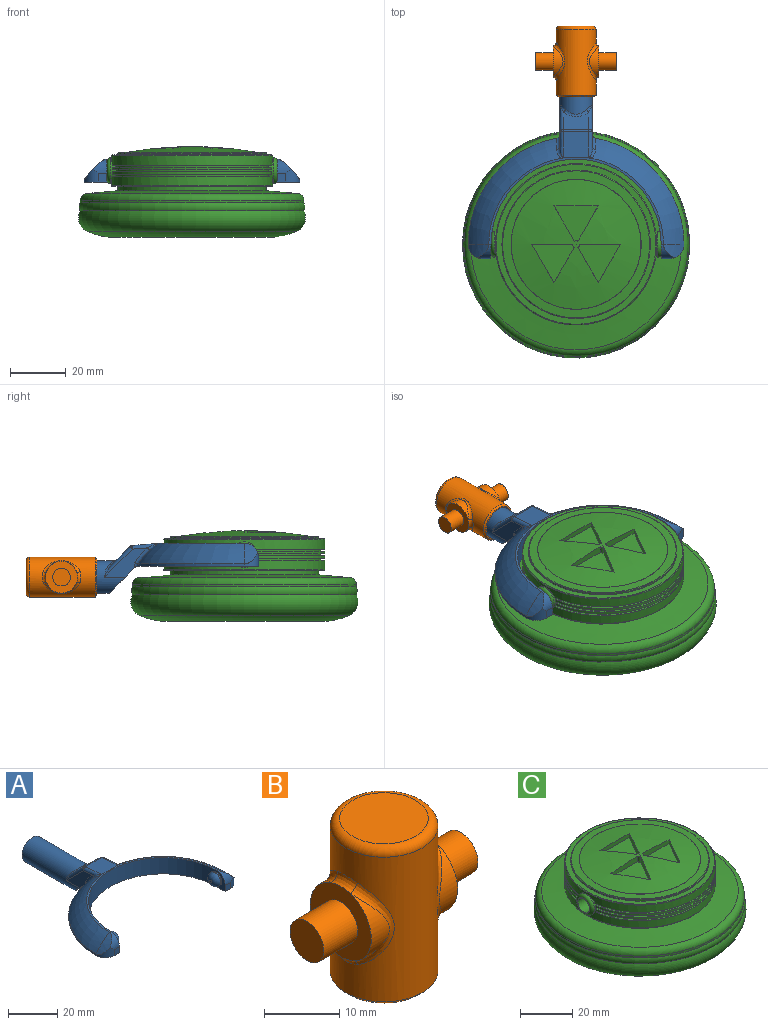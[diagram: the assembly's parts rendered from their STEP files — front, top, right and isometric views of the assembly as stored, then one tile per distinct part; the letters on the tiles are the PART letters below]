
ASSEMBLY  parts=3 mates=2
PART A: 48 faces, bbox 77.3x80.8x18.2 mm
  f0: plane 11.99x9.83mm, normal (0,-0.71,-0.71), area 141.5mm2, adj f1,f2,f9,f30,f43,f46
  f1: plane 15.39x10.49mm, normal (-1,0,0), area 63.5mm2, adj f0,f30,f32,f36,f46,f47
  f2: plane 15.39x10.49mm, normal (1,0,0), area 63.5mm2, adj f0,f30,f34,f39,f43,f44
  f3: plane 9.14x6.37mm, normal (0,0.71,0.71), area 67.6mm2, adj f35,f36,f39,f40
  f4: cylinder r=38.61mm len=37.99mm, axis (0,0,-1), area 42.6mm2, adj f6,f9,f17,f46,f47
  f5: torus R=19.3mm, axis (0,0,-1), area 507.8mm2, adj f10,f11,f12,f29,f42,f44
  f6: torus R=19.3mm, axis (0,0,-1), area 507.8mm2, adj f4,f11,f15,f28,f45,f47
  f7: cylinder r=30.48mm len=60.96mm, axis (0,0,-1), area 746.6mm2, adj f8,f9,f11,f14,f21,f24
  f8: plane 8.13x5.08mm, normal (-1,0,0), area 19.9mm2, adj f7,f9,f13,f19,f24
  f9: plane 77.22x43.73mm, normal (0,0,-1), area 956.2mm2, adj f0,f4,f7,f8,f10,f13,f14,f16
  f10: cylinder r=38.61mm len=37.99mm, axis (0,0,-1), area 42.6mm2, adj f5,f9,f20,f43,f44
  f11: plane 62.55x30.95mm, normal (0,0,1), area 75mm2, adj f5,f6,f7,f18,f19,f27
  f12: cylinder r=22.71mm len=7.33mm, axis (0,1,0), area 24.8mm2, adj f5,f19,f20
  f13: plane 3.05x3.05mm, normal (0,-1,0), area 9.3mm2, adj f8,f9,f19,f20
  f14: plane 8.13x5.08mm, normal (1,0,0), area 19.9mm2, adj f7,f9,f16,f18,f21
  f15: cylinder r=22.71mm len=7.33mm, axis (0,1,0), area 24.8mm2, adj f6,f17,f18
  f16: plane 3.05x3.05mm, normal (0,-1,0), area 9.3mm2, adj f9,f14,f17,f18
  f17: cylinder r=5.08mm len=5.08mm, axis (0,0,-1), area 21.9mm2, adj f4,f9,f15,f16,f18
  f18: cylinder r=5.08mm len=5.08mm, axis (-1,0,0), area 21.9mm2, adj f11,f14,f15,f16,f17
  f19: cylinder r=5.08mm len=5.08mm, axis (-1,0,0), area 21.9mm2, adj f8,f11,f12,f13,f20
  f20: cylinder r=5.08mm len=5.08mm, axis (0,0,-1), area 21.9mm2, adj f9,f10,f12,f13,f19
  f21: cylinder r=3.17mm len=6.35mm, axis (-1,0,0), area 12.7mm2, adj f7,f14,f23
  f22: plane 1.27x1.27mm, normal (1,0,0), area 1.3mm2, adj f23
  f23: torus R=0.64mm, axis (1,0,0), area 56.5mm2, adj f21,f22
  f24: cylinder r=3.17mm len=6.35mm, axis (1,0,0), area 12.7mm2, adj f7,f8,f26
  f25: plane 1.27x1.27mm, normal (-1,0,0), area 1.3mm2, adj f26
  f26: torus R=0.64mm, axis (-1,0,0), area 56.5mm2, adj f24,f25
  f27: plane 9.86x9.36mm, normal (0,0.09,1), area 85.6mm2, adj f11,f28,f29,f32,f34,f35,f42,f45
  f28: plane 1.04x0.17mm, normal (0,-1,0), area 0mm2, adj f6,f27,f45
  f29: plane 1.04x0.17mm, normal (0,-1,0), area 0mm2, adj f5,f27,f42
  f30: cylinder r=5.84mm len=33.01mm, axis (0,-1,0), area 1029.7mm2, adj f0,f1,f2,f31,f38,f40,f41
  f31: plane 11.68x11.68mm, normal (0,1,0), area 107.2mm2, adj f30
  f32: cylinder r=1.27mm len=9.13mm, axis (0,-1,0.09), area 14.4mm2, adj f1,f27,f33,f45
  f33: sphere r=1.27mm, area 1.5mm2, adj f32,f35,f36
  f34: cylinder r=1.27mm len=9.13mm, axis (0,1,-0.09), area 14.4mm2, adj f2,f27,f37,f42
  f35: cylinder r=1.27mm len=9.14mm, axis (-1,0,0), area 8.1mm2, adj f3,f27,f33,f37
  f36: cylinder r=1.27mm len=10.91mm, axis (0,-0.71,0.71), area 23.1mm2, adj f1,f3,f33,f38
  f37: sphere r=1.27mm, area 1.5mm2, adj f34,f35,f39
  f38: bspline ~4.55x2.75mm, area 2.3mm2, adj f30,f36,f40
  f39: cylinder r=1.27mm len=10.91mm, axis (0,0.71,-0.71), area 23.1mm2, adj f2,f3,f37,f41
  f40: bspline ~9.14x2.56mm, area 10.7mm2, adj f3,f30,f38,f41
  f41: bspline ~5.23x3.53mm, area 2.3mm2, adj f30,f39,f40
  f42: bspline ~4.62x3.14mm, area 5.2mm2, adj f5,f27,f29,f34,f44
  f43: cylinder r=1.27mm len=1.74mm, axis (0,0,-1), area 1.9mm2, adj f0,f2,f9,f10,f44
  f44: bspline ~8.6x7.86mm, area 11.9mm2, adj f2,f5,f10,f42,f43
  f45: bspline ~4.62x3.14mm, area 5.2mm2, adj f6,f27,f28,f32,f47
  f46: cylinder r=1.27mm len=1.74mm, axis (0,0,-1), area 1.9mm2, adj f0,f1,f4,f9,f47
  f47: bspline ~8.6x7.86mm, area 11.9mm2, adj f1,f4,f6,f45,f46
PART B: 25 faces, bbox 28.9x15.5x25.4 mm
  f0: cylinder r=5.71mm len=10.81mm, axis (-1,0,0), area 26.2mm2, adj f5,f15
  f1: cylinder r=5.71mm len=10.81mm, axis (-1,0,0), area 26.2mm2, adj f8,f11
  f2: cylinder r=7.14mm len=23.5mm, axis (0,0,-1), area 763.2mm2, adj f9,f10,f11,f12,f13,f14,f15,f16
  f3: plane 11.75x11.75mm, normal (0,0,1), area 108.4mm2, adj f17
  f4: plane 13.02x13.02mm, normal (0,0,-1), area 16.3mm2, adj f22,f24
  f5: plane 11.46x11.46mm, normal (1,0,0), area 70.9mm2, adj f0,f6,f13,f16,f18
  f6: cylinder r=5.71mm len=10.81mm, axis (-1,0,0), area 26.2mm2, adj f5,f14
  f7: cylinder r=5.71mm len=10.81mm, axis (-1,0,0), area 26.2mm2, adj f8,f10
  f8: plane 11.46x11.46mm, normal (-1,0,0), area 70.9mm2, adj f1,f7,f9,f12,f20
  f9: bspline ~4.64x1.73mm, area 6.5mm2, adj f2,f8,f10,f11
  f10: bspline ~13.62x4.91mm, area 20.7mm2, adj f2,f7,f9,f12
  f11: bspline ~13.6x4.87mm, area 20.7mm2, adj f1,f2,f9,f12
  f12: bspline ~4.64x1.73mm, area 6.5mm2, adj f2,f8,f10,f11
  f13: bspline ~4.64x1.73mm, area 6.5mm2, adj f2,f5,f14,f15
  f14: bspline ~13.62x4.91mm, area 20.7mm2, adj f2,f6,f13,f16
  f15: bspline ~13.6x4.87mm, area 20.7mm2, adj f0,f2,f13,f16
  f16: bspline ~4.64x1.73mm, area 6.5mm2, adj f2,f5,f14,f15
  f17: torus R=5.87mm, axis (0,0,1), area 83.8mm2, adj f2,f3
  f18: cylinder r=3.17mm len=6.35mm, axis (-1,0,0), area 126.7mm2, adj f5,f19
  f19: plane 6.35x6.35mm, normal (1,0,0), area 31.7mm2, adj f18
  f20: cylinder r=3.17mm len=6.35mm, axis (1,0,0), area 126.7mm2, adj f8,f21
  f21: plane 6.35x6.35mm, normal (-1,0,0), area 31.7mm2, adj f20
  f22: cylinder r=6.1mm len=22.86mm, axis (0,0,-1), area 875.6mm2, adj f4,f23
  f23: plane 12.19x12.19mm, normal (0,0,-1), area 116.7mm2, adj f22
  f24: cone r=7.14mm half-angle=45deg, axis (0,0,1), area 38.5mm2, adj f2,f4
PART C: 64 faces, bbox 96.2x96.2x32.5 mm
  f0: cylinder r=28.87mm len=57.73mm, axis (0,0,-1), area 595.7mm2, adj f1,f2,f54,f55,f60
  f1: plane 57.13x24.71mm, normal (0,0,1), area 102mm2, adj f0,f3,f54,f55
  f2: plane 57.13x24.71mm, normal (0,0,1), area 102mm2, adj f0,f4,f54,f55
  f3: cylinder r=27.6mm len=54.56mm, axis (0,0,-1), area 49.6mm2, adj f1,f6,f54,f55
  f4: cylinder r=27.6mm len=54.56mm, axis (0,0,-1), area 49.6mm2, adj f2,f5,f54,f55
  f5: plane 57.06x24.48mm, normal (0,0,-1), area 101.4mm2, adj f4,f8,f54,f55
  f6: plane 57.06x24.48mm, normal (0,0,-1), area 101.4mm2, adj f3,f7,f54,f55
  f7: cylinder r=28.87mm len=57.06mm, axis (0,0,-1), area 77.8mm2, adj f6,f9,f54,f55
  f8: cylinder r=28.87mm len=57.06mm, axis (0,0,-1), area 77.8mm2, adj f5,f10,f54,f55
  f9: plane 57.01x24.31mm, normal (0,0,1), area 101mm2, adj f7,f11,f54,f55
  f10: plane 57.01x24.31mm, normal (0,0,1), area 101mm2, adj f8,f12,f54,f55
  f11: cylinder r=27.6mm len=54.44mm, axis (0,0,-1), area 49.2mm2, adj f9,f13,f54,f55
  f12: cylinder r=27.6mm len=54.44mm, axis (0,0,-1), area 49.2mm2, adj f10,f14,f54,f55
  f13: plane 57.01x24.31mm, normal (0,0,-1), area 101mm2, adj f11,f15,f54,f55
  f14: plane 57.01x24.31mm, normal (0,0,-1), area 101mm2, adj f12,f16,f54,f55
  f15: cylinder r=28.87mm len=57.06mm, axis (0,0,-1), area 77.8mm2, adj f13,f22,f54,f55
  f16: cylinder r=28.87mm len=57.06mm, axis (0,0,-1), area 77.8mm2, adj f14,f21,f54,f55
  f17: cylinder r=27.6mm len=54.56mm, axis (0,0,-1), area 49.6mm2, adj f19,f22,f54,f55
  f18: cylinder r=27.6mm len=54.56mm, axis (0,0,-1), area 49.6mm2, adj f20,f21,f54,f55
  f19: plane 57.13x24.71mm, normal (0,0,-1), area 102mm2, adj f17,f23,f54,f55
  f20: plane 57.13x24.71mm, normal (0,0,-1), area 102mm2, adj f18,f23,f54,f55
  f21: plane 57.06x24.48mm, normal (0,0,1), area 101.4mm2, adj f16,f18,f54,f55
  f22: plane 57.06x24.48mm, normal (0,0,1), area 101.4mm2, adj f15,f17,f54,f55
  f23: cylinder r=28.87mm len=57.73mm, axis (0,0,-1), area 595.8mm2, adj f19,f20,f54,f55,f61
  f24: sphere r=135.39mm, area 1385.3mm2, adj f38,f39,f40,f41,f43,f44,f45,f46
  f25: plane 39.3x39.3mm, normal (0,0,-1), area 1213mm2, adj f26
  f26: torus R=20.1mm, axis (0,0,-1), area 1428.2mm2, adj f25,f27
  f27: torus R=27.72mm, axis (0,0,-1), area 3540.4mm2, adj f26,f28
  f28: torus R=35.34mm, axis (0,0,-1), area 2179.4mm2, adj f27,f29
  f29: torus R=37.33mm, axis (0,0,-1), area 734.3mm2, adj f28,f30
  f30: cylinder r=40.04mm len=80.09mm, axis (0,0,-1), area 213.2mm2, adj f29,f34
  f31: cone r=26.57mm half-angle=85deg, axis (0,0,-1), area 2261.9mm2, adj f32,f34
  f32: cylinder r=26.57mm len=53.14mm, axis (0,0,-1), area 265mm2, adj f31,f33
  f33: plane 57.23x57.23mm, normal (0,0,-1), area 354.5mm2, adj f32,f60
  f34: torus R=37.5mm, axis (0,0,1), area 928.3mm2, adj f30,f31
  f35: cone r=26.57mm half-angle=87deg, axis (0,0,-1), area 475.4mm2, adj f62,f63
  f36: cylinder r=26.57mm len=53.14mm, axis (0,0,-1), area 92.3mm2, adj f37,f62
  f37: plane 57.23x57.23mm, normal (0,0,1), area 354.5mm2, adj f36,f61
  f38: plane 12.65x7.3mm, normal (-0.87,0.5,0), area 32.2mm2, adj f24,f39,f41,f42
  f39: cylinder r=1.27mm len=2.53mm, axis (0,0,1), area 3.4mm2, adj f24,f38,f40,f42
  f40: plane 14.61x2.53mm, normal (0,-1,0), area 32.2mm2, adj f24,f39,f41,f42
  f41: plane 13.75x7.94mm, normal (0.87,0.5,0), area 28mm2, adj f24,f38,f40,f42
  f42: plane 15.24x13.75mm, normal (0,0,1), area 108.3mm2, adj f38,f39,f40,f41
  f43: cylinder r=1.27mm len=2.53mm, axis (0,0,1), area 3.4mm2, adj f24,f44,f46,f47
  f44: plane 12.65x7.3mm, normal (0.87,0.5,0), area 32.2mm2, adj f24,f43,f45,f47
  f45: plane 13.75x7.94mm, normal (-0.87,0.5,0), area 28mm2, adj f24,f44,f46,f47
  f46: plane 14.61x2.53mm, normal (0,-1,0), area 32.2mm2, adj f24,f43,f45,f47
  f47: plane 15.24x13.75mm, normal (0,0,1), area 108.3mm2, adj f43,f44,f45,f46
  f48: plane 15.88x1.84mm, normal (0,-1,0), area 28mm2, adj f24,f49,f51,f52
  f49: plane 12.65x7.3mm, normal (0.87,0.5,0), area 32.2mm2, adj f24,f48,f50,f52
  f50: cylinder r=1.27mm len=2.53mm, axis (0,0,1), area 3.4mm2, adj f24,f49,f51,f52
  f51: plane 12.65x7.3mm, normal (-0.87,0.5,0), area 32.2mm2, adj f24,f48,f50,f52
  f52: plane 15.88x12.65mm, normal (0,0,1), area 108.3mm2, adj f48,f49,f50,f51
  f53: plane 6.6x6.6mm, normal (1,0,0), area 2.6mm2, adj f58,f59
  f54: cylinder r=4.57mm len=9.14mm, axis (-1,0,0), area 20.2mm2, adj f0,f1,f2,f3,f4,f5,f6,f7
  f55: cylinder r=4.57mm len=9.14mm, axis (-1,0,0), area 20.2mm2, adj f0,f1,f2,f3,f4,f5,f6,f7
  f56: plane 6.6x6.6mm, normal (-1,0,0), area 2.6mm2, adj f57,f59
  f57: torus R=3.3mm, axis (1,0,0), area 51.5mm2, adj f55,f56
  f58: torus R=3.3mm, axis (1,0,0), area 51.5mm2, adj f53,f54
  f59: cylinder r=3.17mm len=60.96mm, axis (1,0,0), area 1216.1mm2, adj f53,f56
  f60: torus R=28.61mm, axis (0,0,1), area 72.1mm2, adj f0,f33
  f61: torus R=28.61mm, axis (0,0,-1), area 72.1mm2, adj f23,f37
  f62: torus R=26.31mm, axis (0,0,1), area 64.2mm2, adj f35,f36
  f63: torus R=23.29mm, axis (0,0,1), area 4.5mm2, adj f24,f35
PLACE A t=(32.34,27.52,20.85)mm
PLACE B rot(axis=(-1,0,0),90deg) t=(32.34,80.3,16.88)mm
PLACE C t=(32.34,27.52,33.52)mm
MATE revolute A.f24 <-> C.f54  axis (-1,0,0) through (62.82,27.52,24.92)mm
MATE revolute B.f2 <-> A.f30  axis (0,-1,0) through (32.34,103.16,16.88)mm
